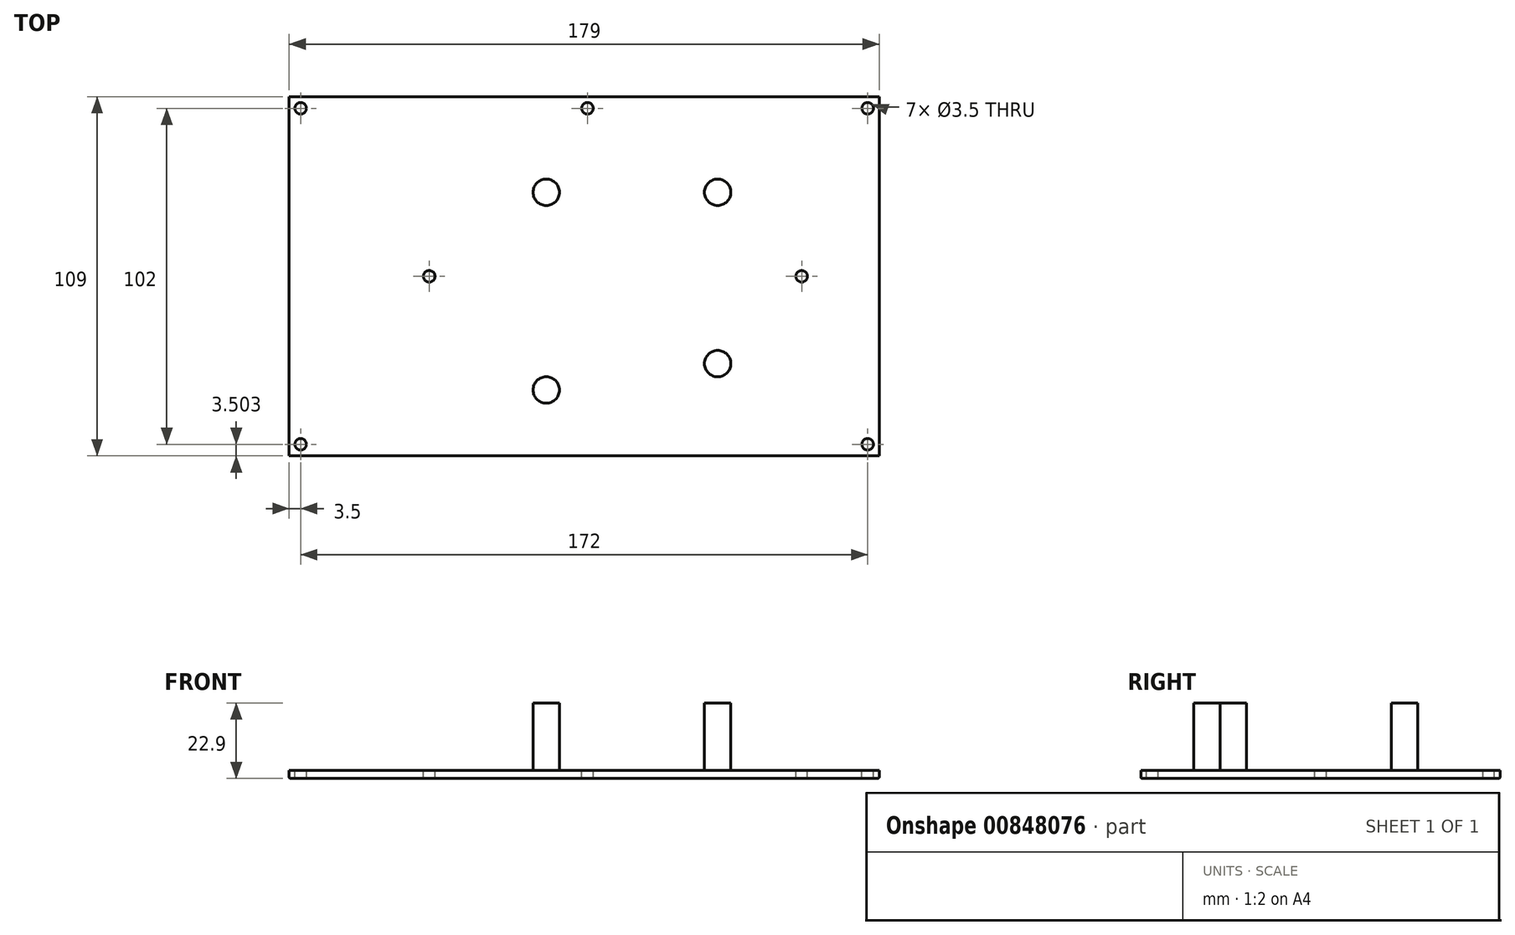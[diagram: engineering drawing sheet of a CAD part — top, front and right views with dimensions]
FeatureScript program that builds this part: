
annotation { "Feature Type Name" : "Feature", "Feature Type Description" : "" }
export const myFeature = defineFeature(function(context is Context, id is Id, definition is map)
    precondition{}
    {
        {
            var Q0;
            Q0=qCreatedBy(makeId("Top.planeOp"),FACE);
            var sketch = newSketch(context, id + "F0", { "sketchPlane" : qUnion([Q0])});
            skLineSegment(sketch, "E0.bottom", {"start": v(-90.5, 54.4) * mm, "end": v(88.5, 54.4) * mm});
            skLineSegment(sketch, "E0.top", {"start": v(-90.5, -54.6) * mm, "end": v(88.5, -54.6) * mm});
            skLineSegment(sketch, "E0.left", {"start": v(-90.5, 54.4) * mm, "end": v(-90.5, -54.6) * mm});
            skLineSegment(sketch, "E0.right", {"start": v(88.5, 54.4) * mm, "end": v(88.5, -54.6) * mm});
            skCircle(sketch, "E1", {"center": v(-87, 50.9) * mm, "radius": 1.75 * mm});
            skCircle(sketch, "E2", {"center": v(85, 50.9) * mm, "radius": 1.75 * mm});
            skCircle(sketch, "E3", {"center": v(85, -51.1) * mm, "radius": 1.75 * mm});
            skCircle(sketch, "E4", {"center": v(-87, -51.1) * mm, "radius": 1.75 * mm});
            skCircle(sketch, "E5", {"center": v(-48, -0.1) * mm, "radius": 1.75 * mm});
            skCircle(sketch, "E6", {"center": v(65, -0.1) * mm, "radius": 1.75 * mm});
            skCircle(sketch, "E7", {"center": v(-12.5, 25.4) * mm, "radius": 4 * mm});
            skCircle(sketch, "E8", {"center": v(39.5, 25.4) * mm, "radius": 4 * mm});
            skCircle(sketch, "E9", {"center": v(-12.5, -34.6) * mm, "radius": 4 * mm});
            skCircle(sketch, "E10", {"center": v(39.5, -26.6) * mm, "radius": 4 * mm});
            skCircle(sketch, "E11", {"center": v(0, 50.9) * mm, "radius": 1.75 * mm});
            skSolve(sketch);
        }
        {
            var Q0;
            Q0 = qSketchRegion(id + "F0", true);
            var Q1;
            Q1=makeQuery(id+"F0.imprint","IMPRINT",FACE,{"disambiguationData":[TD([[makeQuery(id+"F0.imprint","IMPRINT",EDGE,{"derivedFrom":sQuery(id+"F0.wireOp",EDGE,"E7")}),1.0]])]});
            var Q2;
            Q2=makeQuery(id+"F0.imprint","IMPRINT",FACE,{"disambiguationData":[TD([[makeQuery(id+"F0.imprint","IMPRINT",EDGE,{"derivedFrom":sQuery(id+"F0.wireOp",EDGE,"E8")}),1.0]])]});
            var Q3;
            Q3=makeQuery(id+"F0.imprint","IMPRINT",FACE,{"disambiguationData":[TD([[makeQuery(id+"F0.imprint","IMPRINT",EDGE,{"derivedFrom":sQuery(id+"F0.wireOp",EDGE,"E9")}),1.0]])]});
            var Q4;
            Q4=makeQuery(id+"F0.imprint","IMPRINT",FACE,{"disambiguationData":[TD([[makeQuery(id+"F0.imprint","IMPRINT",EDGE,{"derivedFrom":sQuery(id+"F0.wireOp",EDGE,"E10")}),1.0]])]});
            extrude(context, id + "F1", {"entities" : qUnion([Q0, Q1, Q2, Q3, Q4]), "depth" : -2.4 * mm, "offsetDistance" : 25 * mm});
        }
        {
            var Q0;
            Q0=makeQuery(id+"F0.imprint","IMPRINT",FACE,{"disambiguationData":[TD([[makeQuery(id+"F0.imprint","IMPRINT",EDGE,{"derivedFrom":sQuery(id+"F0.wireOp",EDGE,"E7")}),1.0]])]});
            var Q1;
            Q1=makeQuery(id+"F0.imprint","IMPRINT",FACE,{"disambiguationData":[TD([[makeQuery(id+"F0.imprint","IMPRINT",EDGE,{"derivedFrom":sQuery(id+"F0.wireOp",EDGE,"E9")}),1.0]])]});
            var Q2;
            Q2=makeQuery(id+"F0.imprint","IMPRINT",FACE,{"disambiguationData":[TD([[makeQuery(id+"F0.imprint","IMPRINT",EDGE,{"derivedFrom":sQuery(id+"F0.wireOp",EDGE,"E10")}),1.0]])]});
            var Q3;
            Q3=makeQuery(id+"F0.imprint","IMPRINT",FACE,{"disambiguationData":[TD([[makeQuery(id+"F0.imprint","IMPRINT",EDGE,{"derivedFrom":sQuery(id+"F0.wireOp",EDGE,"E8")}),1.0]])]});
            extrude(context, id + "F2", {"entities" : qUnion([Q0, Q1, Q2, Q3]), "operationType" : NewBodyOperationType.ADD, "depth" : 20.5 * mm, "offsetDistance" : 25 * mm});
        }
        {
            var Q0;
            Q0=makeQuery(id+"F1.opExtrude","CAP_EDGE",EDGE,{"disambiguationData":[OSD([sQuery(id+"F0.wireOp",EDGE,"E0.bottom")])],"isStart":false});
            var Q1;
            Q1=makeQuery(id+"F1.opExtrude","CAP_EDGE",EDGE,{"disambiguationData":[OSD([sQuery(id+"F0.wireOp",EDGE,"E0.left")])],"isStart":false});
            var Q2;
            Q2=makeQuery(id+"F1.opExtrude","CAP_EDGE",EDGE,{"disambiguationData":[OSD([sQuery(id+"F0.wireOp",EDGE,"E0.right")])],"isStart":false});
            var Q3;
            Q3=makeQuery(id+"F1.opExtrude","CAP_EDGE",EDGE,{"disambiguationData":[OSD([sQuery(id+"F0.wireOp",EDGE,"E0.top")])],"isStart":false});
            fillet(context, id + "F3", {"entities" : qUnion([Q0, Q1, Q2, Q3]), "radius" : 0.4 * mm, "tangentPropagation" : true, "allowEdgeOverflow" : false});
        }
    });
